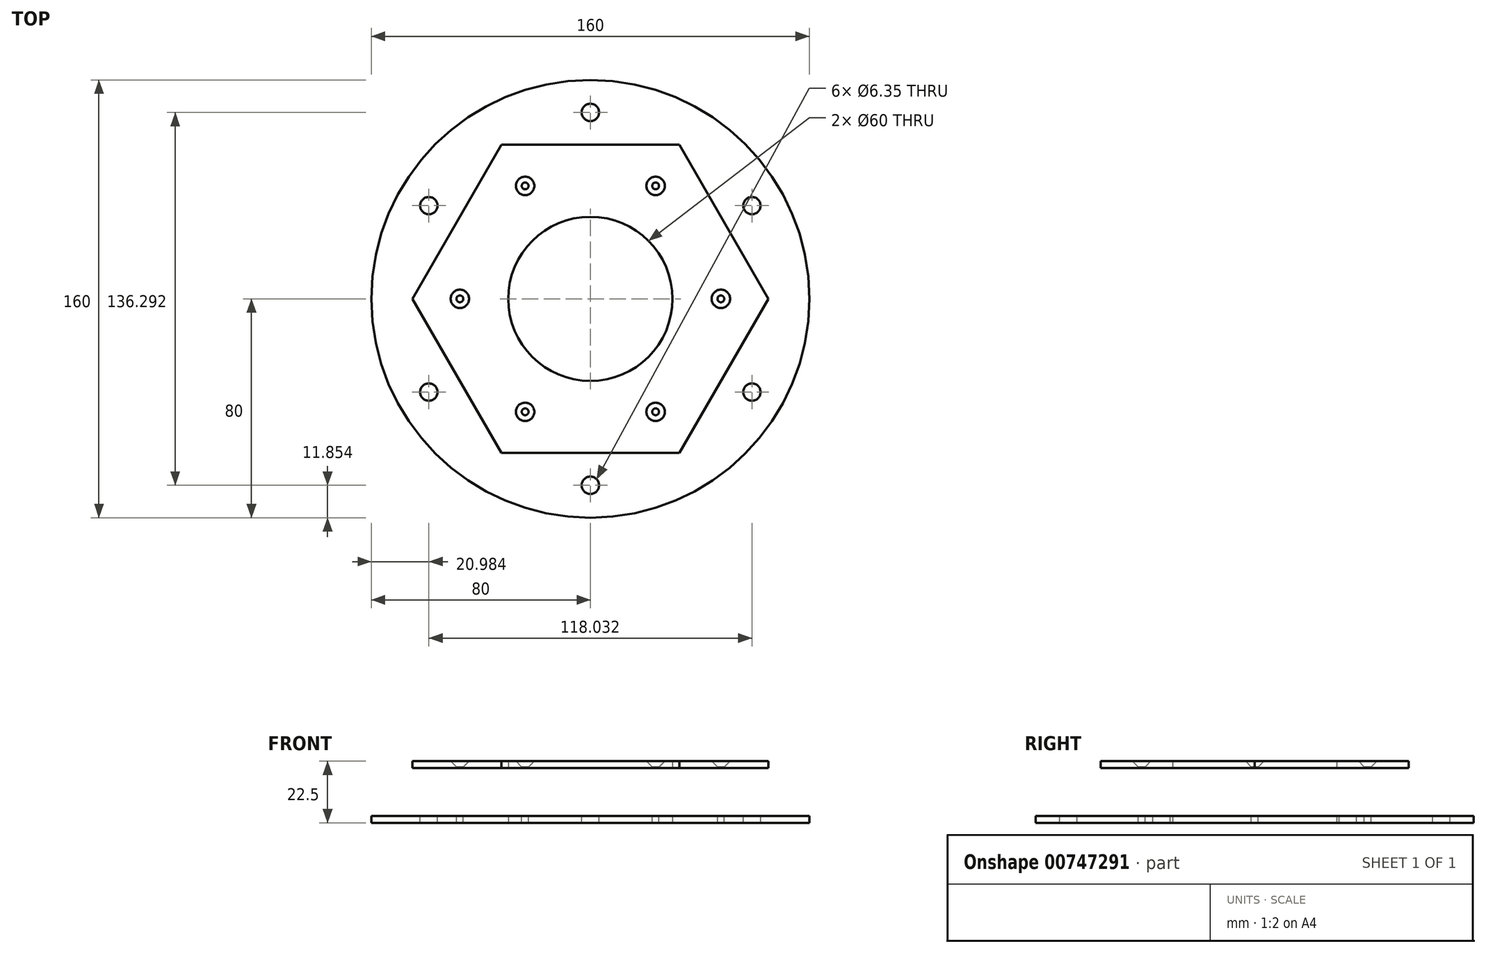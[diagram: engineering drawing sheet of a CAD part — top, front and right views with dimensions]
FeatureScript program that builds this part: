
annotation { "Feature Type Name" : "Feature", "Feature Type Description" : "" }
export const myFeature = defineFeature(function(context is Context, id is Id, definition is map)
    precondition{}
    {
        {
            var Q0;
            Q0=qCreatedBy(makeId("Top.planeOp"),FACE);
            var sketch = newSketch(context, id + "F0", { "sketchPlane" : qUnion([Q0])});
            skCircle(sketch, "E0.cCircle", {"center": v(0, 0) * mm, "radius": 56.3 * mm, "construction": true});
            skLineSegment(sketch, "E0.0", {"start": v(32.5, 56.3) * mm, "end": v(65, 0) * mm});
            skLineSegment(sketch, "E0.1", {"start": v(65, 0) * mm, "end": v(32.5, -56.3) * mm});
            skLineSegment(sketch, "E0.2", {"start": v(32.5, -56.3) * mm, "end": v(-32.5, -56.3) * mm});
            skLineSegment(sketch, "E0.3", {"start": v(-32.5, -56.3) * mm, "end": v(-65, 0) * mm});
            skLineSegment(sketch, "E0.4", {"start": v(-65, 0) * mm, "end": v(-32.5, 56.3) * mm});
            skLineSegment(sketch, "E0.5", {"start": v(-32.5, 56.3) * mm, "end": v(32.5, 56.3) * mm});
            skPoint(sketch, "E0.0.midPoint", {"position": v(48.75, 28.15) * mm});
            skPoint(sketch, "E1.0.midPoint", {"position": v(31.43, 18.15) * mm});
            skLineSegment(sketch, "E2", {"start": v(-32.5, 56.3) * mm, "end": v(-20.95, 36.3) * mm, "construction": true});
            skLineSegment(sketch, "E3", {"start": v(32.5, 56.3) * mm, "end": v(20.95, 36.3) * mm, "construction": true});
            skLineSegment(sketch, "E4", {"start": v(65, 0) * mm, "end": v(41.9, 0) * mm, "construction": true});
            skLineSegment(sketch, "E5", {"start": v(20.95, -36.3) * mm, "end": v(32.5, -56.3) * mm, "construction": true});
            skLineSegment(sketch, "E6", {"start": v(-20.95, -36.3) * mm, "end": v(-32.5, -56.3) * mm, "construction": true});
            skLineSegment(sketch, "E7", {"start": v(-41.9, 0) * mm, "end": v(-65, 0) * mm, "construction": true});
            skCircle(sketch, "E8", {"center": v(0, 0) * mm, "radius": 80 * mm});
            skCircle(sketch, "E9", {"center": v(0, 0) * mm, "radius": 30 * mm});
            skSolve(sketch);
        }
        {
            var Q0;
            Q0=qSketchRegion(id+"F0",true);
            var Q1;
            Q1=makeQuery(id+"F0.imprint","IMPRINT",FACE,{"disambiguationData":[TD([[makeQuery(id+"F0.imprint","IMPRINT",EDGE,{"derivedFrom":sQuery(id+"F0.wireOp",EDGE,"E0.0")}),-1.0]])]});
            extrude(context, id + "F1", {"entities" : qUnion([Q0, Q1]), "depth" : 2.5 * mm, "offsetDistance" : 25 * mm});
        }
        {
            var Q0;
            Q0=qCreatedBy(makeId("Top.planeOp"),FACE);
            cPlane(context, id + "F2", {"entities" : qUnion([Q0]), "cplaneType" : CPlaneType.OFFSET, "offset" : 20 * mm, "width" : 150 * mm, "height" : 150 * mm});
        }
        {
            var Q0;
            Q0=qCreatedBy(id+"F2.planeOp",FACE);
            var sketch = newSketch(context, id + "F3", { "sketchPlane" : qUnion([Q0])});
            skCircle(sketch, "E10.cCircle", {"center": v(0, 0) * mm, "radius": 56.3 * mm, "construction": true});
            skLineSegment(sketch, "E10.0", {"start": v(32.5, 56.3) * mm, "end": v(65, 0) * mm});
            skLineSegment(sketch, "E10.1", {"start": v(65, 0) * mm, "end": v(32.5, -56.3) * mm});
            skLineSegment(sketch, "E10.2", {"start": v(32.5, -56.3) * mm, "end": v(-32.5, -56.3) * mm});
            skLineSegment(sketch, "E10.3", {"start": v(-32.5, -56.3) * mm, "end": v(-65, 0) * mm});
            skLineSegment(sketch, "E10.4", {"start": v(-65, 0) * mm, "end": v(-32.5, 56.3) * mm});
            skLineSegment(sketch, "E10.5", {"start": v(-32.5, 56.3) * mm, "end": v(32.5, 56.3) * mm});
            skPoint(sketch, "E10.0.midPoint", {"position": v(48.75, 28.15) * mm});
            skPoint(sketch, "E11.0.midPoint", {"position": v(31.43, -18.15) * mm});
            skCircle(sketch, "E12", {"center": v(0, 0) * mm, "radius": 30 * mm});
            skSolve(sketch);
        }
        {
            var Q0;
            Q0=qSketchRegion(id+"F3",true);
            extrude(context, id + "F4", {"entities" : qUnion([Q0]), "depth" : 2.5 * mm, "offsetDistance" : 25 * mm});
        }
        {
            var Q0;
            Q0=makeQuery(id+"F4.opExtrude","CAP_FACE",FACE,{"disambiguationData":[OSD([sQuery(id+"F3.wireOp",EDGE,"E10.0"),sQuery(id+"F3.wireOp",EDGE,"E10.1"),sQuery(id+"F3.wireOp",EDGE,"E10.2"),sQuery(id+"F3.wireOp",EDGE,"E10.3"),sQuery(id+"F3.wireOp",EDGE,"E10.4"),sQuery(id+"F3.wireOp",EDGE,"E10.5"),sQuery(id+"F3.wireOp",EDGE,"E11.0"),sQuery(id+"F3.wireOp",EDGE,"E11.1"),sQuery(id+"F3.wireOp",EDGE,"E11.2"),sQuery(id+"F3.wireOp",EDGE,"E11.3"),sQuery(id+"F3.wireOp",EDGE,"E11.4"),sQuery(id+"F3.wireOp",EDGE,"E11.5")])],"isStart":false});
            var sketch = newSketch(context, id + "F5", { "sketchPlane" : qUnion([Q0])});
            skLineSegment(sketch, "E13", {"start": v(-32.5, 56.3) * mm, "end": v(-15.18, 26.3) * mm, "construction": true});
            skLineSegment(sketch, "E14", {"start": v(32.5, 56.3) * mm, "end": v(15.18, 26.3) * mm, "construction": true});
            skLineSegment(sketch, "E15", {"start": v(65, 0) * mm, "end": v(30.36, 0) * mm, "construction": true});
            skLineSegment(sketch, "E16", {"start": v(32.5, -56.3) * mm, "end": v(15.18, -26.3) * mm, "construction": true});
            skLineSegment(sketch, "E17", {"start": v(-32.5, -56.3) * mm, "end": v(-15.18, -26.3) * mm, "construction": true});
            skLineSegment(sketch, "E18", {"start": v(-65, 0) * mm, "end": v(-30.36, 0) * mm, "construction": true});
            skPoint(sketch, "E19", {"position": v(-23.84, 41.3) * mm});
            skPoint(sketch, "E20", {"position": v(23.84, 41.3) * mm});
            skPoint(sketch, "E21", {"position": v(47.68, 0) * mm});
            skPoint(sketch, "E22", {"position": v(23.84, -41.3) * mm});
            skPoint(sketch, "E23", {"position": v(-23.84, -41.3) * mm});
            skPoint(sketch, "E24", {"position": v(-47.68, 0) * mm});
            skSolve(sketch);
        }
        {
            var Q0;
            Q0=sQuery(id+"F5.wireOp",VERTEX,"E19");
            var Q1;
            Q1=sQuery(id+"F5.wireOp",VERTEX,"E20");
            var Q2;
            Q2=sQuery(id+"F5.wireOp",VERTEX,"E21");
            var Q3;
            Q3=sQuery(id+"F5.wireOp",VERTEX,"E22");
            var Q4;
            Q4=sQuery(id+"F5.wireOp",VERTEX,"E23");
            var Q5;
            Q5=sQuery(id+"F5.wireOp",VERTEX,"E24");
            var Q6;
            Q6=makeQuery(id+"F4.opExtrude","SWEPT_BODY",BODY,{"disambiguationData":[OSD([sQuery(id+"F3.wireOp",EDGE,"E10.0"),sQuery(id+"F3.wireOp",EDGE,"E10.1"),sQuery(id+"F3.wireOp",EDGE,"E10.2"),sQuery(id+"F3.wireOp",EDGE,"E10.3"),sQuery(id+"F3.wireOp",EDGE,"E10.4"),sQuery(id+"F3.wireOp",EDGE,"E10.5"),sQuery(id+"F3.wireOp",EDGE,"E12")])]});
            var Q7;
            Q7=makeQuery(id+"F1.opExtrude","SWEPT_BODY",BODY,{"disambiguationData":[OSD([sQuery(id+"F0.wireOp",EDGE,"E8"),sQuery(id+"F0.wireOp",EDGE,"E9")])]});
            hole(context, id + "F6", {"style" : HoleStyle.C_SINK, "endStyle" : HoleEndStyle.THROUGH, "standardTappedOrClearance" : lookupTablePath({ "standard" : "ISO", "engagement" : "75%", "pitch" : "0.5 mm", "size" : "M3", "type" : "Tapped" }), "standardBlindInLast" : lookupTablePath({ "standard" : "ISO", "engagement" : "75%", "pitch" : "0.5 mm", "size" : "M3", "type" : "Tapped" }), "holeDiameter" : 2.5 * mm, "cSinkDiameter" : 6.72 * mm, "cSinkAngle" : 90 * degree, "majorDiameter" : 3 * mm, "showTappedDepth" : true, "isTappedThrough" : true, "tappedDepth" : 12 * mm, "tapClearance" : 3, "locations" : qUnion([Q0, Q1, Q2, Q3, Q4, Q5]), "scope" : qUnion([Q6, Q7])});
        }
        {
            var Q0;
            Q0=makeQuery(id+"F1.opExtrude","CAP_FACE",FACE,{"disambiguationData":[OSD([sQuery(id+"F0.wireOp",EDGE,"E1.0"),sQuery(id+"F0.wireOp",EDGE,"E1.1"),sQuery(id+"F0.wireOp",EDGE,"E1.2"),sQuery(id+"F0.wireOp",EDGE,"E1.3"),sQuery(id+"F0.wireOp",EDGE,"E1.4"),sQuery(id+"F0.wireOp",EDGE,"E1.5"),sQuery(id+"F0.wireOp",EDGE,"E8")])],"isStart":false});
            var sketch = newSketch(context, id + "F7", { "sketchPlane" : qUnion([Q0])});
            skCircle(sketch, "E25", {"center": v(0, 0) * mm, "radius": 80 * mm, "construction": true});
            skCircle(sketch, "E26.cCircle", {"center": v(0, 0) * mm, "radius": 56.3 * mm, "construction": true});
            skLineSegment(sketch, "E26.0", {"start": v(32.5, 56.3) * mm, "end": v(65, 0) * mm, "construction": true});
            skLineSegment(sketch, "E26.1", {"start": v(65, 0) * mm, "end": v(32.5, -56.3) * mm, "construction": true});
            skLineSegment(sketch, "E26.2", {"start": v(32.5, -56.3) * mm, "end": v(-32.5, -56.3) * mm, "construction": true});
            skLineSegment(sketch, "E26.3", {"start": v(-32.5, -56.3) * mm, "end": v(-65, 0) * mm, "construction": true});
            skLineSegment(sketch, "E26.4", {"start": v(-65, 0) * mm, "end": v(-32.5, 56.3) * mm, "construction": true});
            skLineSegment(sketch, "E26.5", {"start": v(-32.5, 56.3) * mm, "end": v(32.5, 56.3) * mm, "construction": true});
            skPoint(sketch, "E26.0.midPoint", {"position": v(48.75, 28.15) * mm});
            skLineSegment(sketch, "E27", {"start": v(0, 56.3) * mm, "end": v(0, 80) * mm, "construction": true});
            skLineSegment(sketch, "E28", {"start": v(48.75, 28.15) * mm, "end": v(69.28, 40) * mm, "construction": true});
            skLineSegment(sketch, "E29", {"start": v(48.75, -28.15) * mm, "end": v(69.28, -40) * mm, "construction": true});
            skLineSegment(sketch, "E30", {"start": v(0, -56.3) * mm, "end": v(0, -80) * mm, "construction": true});
            skLineSegment(sketch, "E31", {"start": v(-48.75, -28.15) * mm, "end": v(-69.28, -40) * mm, "construction": true});
            skLineSegment(sketch, "E32", {"start": v(-48.75, 28.15) * mm, "end": v(-69.28, 40) * mm, "construction": true});
            skPoint(sketch, "E33", {"position": v(0, 68.15) * mm});
            skPoint(sketch, "E34", {"position": v(59.02, 34.07) * mm});
            skPoint(sketch, "E35", {"position": v(59.02, -34.07) * mm});
            skPoint(sketch, "E36", {"position": v(0, -68.15) * mm});
            skPoint(sketch, "E37", {"position": v(-59.02, 34.07) * mm});
            skPoint(sketch, "E38", {"position": v(-59.02, -34.07) * mm});
            skSolve(sketch);
        }
        {
            var Q0;
            Q0=sQuery(id+"F7.wireOp",VERTEX,"E33");
            var Q1;
            Q1=sQuery(id+"F7.wireOp",VERTEX,"E34");
            var Q2;
            Q2=sQuery(id+"F7.wireOp",VERTEX,"E35");
            var Q3;
            Q3=sQuery(id+"F7.wireOp",VERTEX,"E36");
            var Q4;
            Q4=sQuery(id+"F7.wireOp",VERTEX,"E38");
            var Q5;
            Q5=sQuery(id+"F7.wireOp",VERTEX,"E37");
            var Q6;
            Q6=makeQuery(id+"F1.opExtrude","SWEPT_BODY",BODY,{"disambiguationData":[OSD([sQuery(id+"F0.wireOp",EDGE,"E1.0"),sQuery(id+"F0.wireOp",EDGE,"E1.1"),sQuery(id+"F0.wireOp",EDGE,"E1.2"),sQuery(id+"F0.wireOp",EDGE,"E1.3"),sQuery(id+"F0.wireOp",EDGE,"E1.4"),sQuery(id+"F0.wireOp",EDGE,"E1.5"),sQuery(id+"F0.wireOp",EDGE,"E8")])]});
            hole(context, id + "F8", {"style" : HoleStyle.SIMPLE, "endStyle" : HoleEndStyle.THROUGH, "holeDiameter" : 6.35 * mm, "majorDiameter" : 5 * mm, "isTappedThrough" : true, "tappedDepth" : 12 * mm, "tapClearance" : 3, "locations" : qUnion([Q0, Q1, Q2, Q3, Q4, Q5]), "scope" : qUnion([Q6])});
        }
    });
